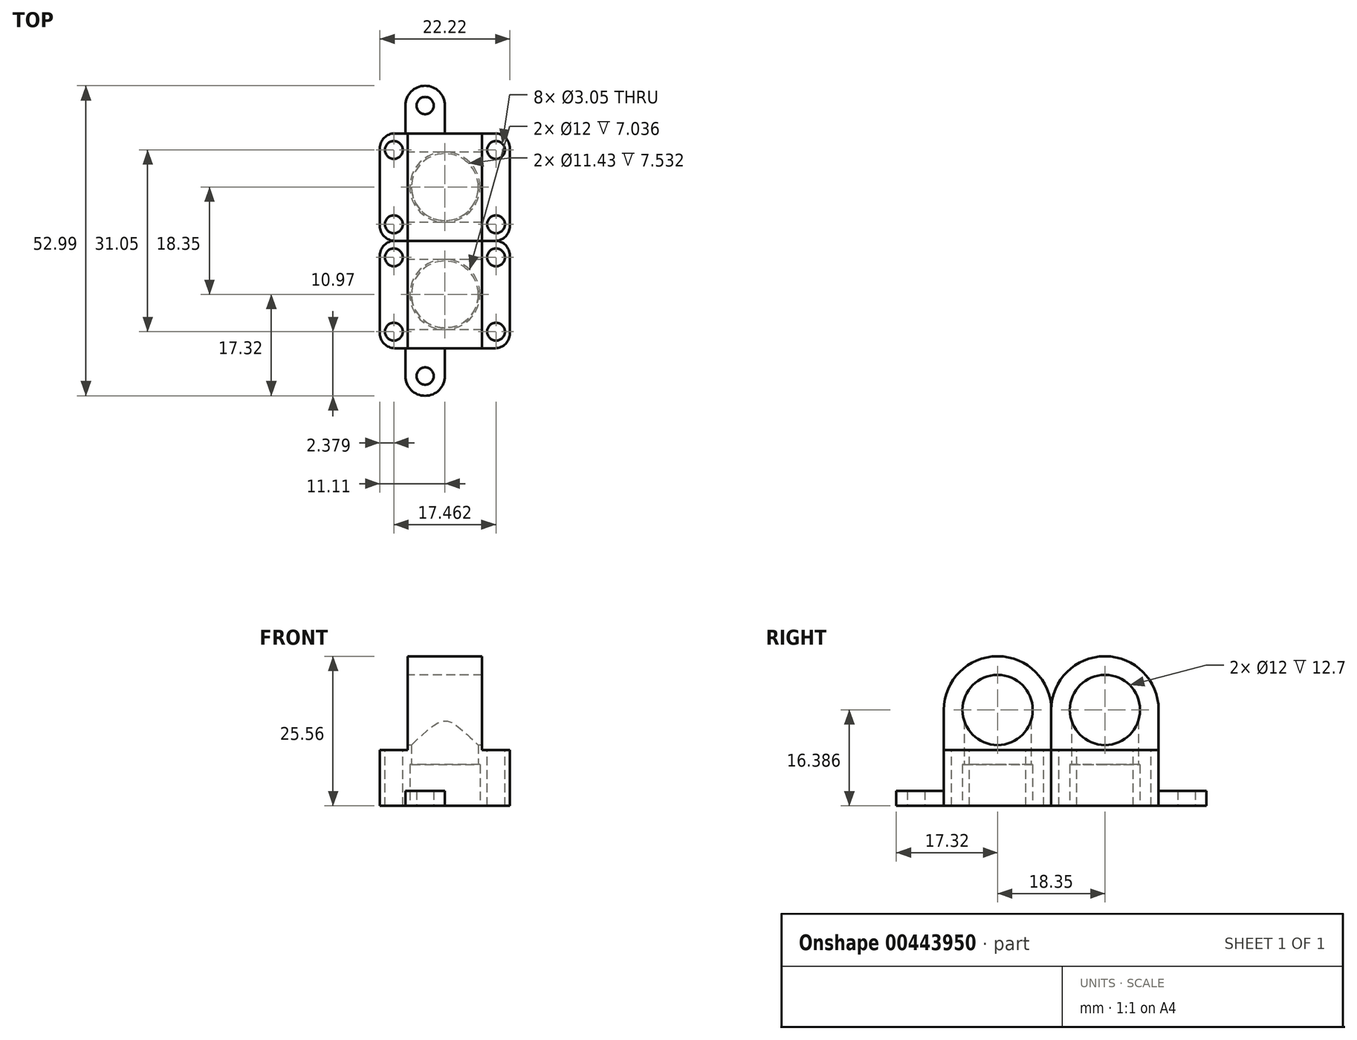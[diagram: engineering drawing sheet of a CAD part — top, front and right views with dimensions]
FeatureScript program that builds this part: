
annotation { "Feature Type Name" : "Feature", "Feature Type Description" : "" }
export const myFeature = defineFeature(function(context is Context, id is Id, definition is map)
    precondition{}
    {
        {
            var Q0;
            Q0=qCreatedBy(makeId("Top.planeOp"),FACE);
            var sketch = newSketch(context, id + "F0", { "sketchPlane" : qUnion([Q0])});
            skCircle(sketch, "E0", {"center": v(0, 0) * mm, "radius": 6 * mm});
            skArc(sketch, "E1", {"start": v(0, 9.18) * mm, "mid": v(9.18, 0) * mm, "end": v(0, -9.18) * mm});
            skLineSegment(sketch, "E2", {"start": v(0, 9.18) * mm, "end": v(-11.11, 9.18) * mm});
            skLineSegment(sketch, "E3", {"start": v(-11.11, 9.18) * mm, "end": v(-11.11, -9.18) * mm});
            skLineSegment(sketch, "E4", {"start": v(-11.11, -9.18) * mm, "end": v(0, -9.18) * mm});
            skSolve(sketch);
        }
        {
            var Q0;
            Q0=qSketchRegion(id+"F0",true);
            extrude(context, id + "F1", {"entities" : qUnion([Q0]), "depth" : 7.04 * mm});
        }
        {
            var Q0;
            Q0=makeQuery(id+"F1.opExtrude","SWEPT_FACE",FACE,{"disambiguationData":[OSD([sQuery(id+"F0.wireOp",EDGE,"E3")])]});
            var sketch = newSketch(context, id + "F2", { "sketchPlane" : qUnion([Q0])});
            skCircle(sketch, "E5", {"center": v(0, 17.8) * mm, "radius": 6 * mm});
            skArc(sketch, "E6", {"start": v(-9.17, 17.8) * mm, "mid": v(0, 26.97) * mm, "end": v(9.17, 17.8) * mm});
            skLineSegment(sketch, "E7", {"start": v(-9.17, 17.8) * mm, "end": v(-9.18, 7.04) * mm});
            skLineSegment(sketch, "E8", {"start": v(-9.18, 7.04) * mm, "end": v(9.17, 7.04) * mm});
            skLineSegment(sketch, "E9", {"start": v(9.17, 7.04) * mm, "end": v(9.17, 17.8) * mm});
            skSolve(sketch);
        }
        {
            var Q0;
            Q0=makeQuery(id+"F1.opExtrude","CAP_FACE",FACE,{"disambiguationData":[OSD([sQuery(id+"F0.wireOp",EDGE,"E0"),sQuery(id+"F0.wireOp",EDGE,"E1"),sQuery(id+"F0.wireOp",EDGE,"E2"),sQuery(id+"F0.wireOp",EDGE,"E3"),sQuery(id+"F0.wireOp",EDGE,"E4")])],"isStart":true});
            var sketch = newSketch(context, id + "F3", { "sketchPlane" : qUnion([Q0])});
            skCircle(sketch, "E10", {"center": v(-3.38, 13.94) * mm, "radius": 1.47 * mm});
            skArc(sketch, "E11", {"start": v(-6.76, 13.94) * mm, "mid": v(-3.38, 17.32) * mm, "end": v(0, 13.94) * mm});
            skLineSegment(sketch, "E12", {"start": v(-6.76, 13.94) * mm, "end": v(-6.76, 9.18) * mm});
            skLineSegment(sketch, "E13", {"start": v(-6.76, 9.18) * mm, "end": v(0, 9.18) * mm});
            skLineSegment(sketch, "E14", {"start": v(0, 9.18) * mm, "end": v(0, 13.94) * mm});
            skSolve(sketch);
        }
        {
            var Q0;
            Q0=qSketchRegion(id+"F3",true);
            extrude(context, id + "F4", {"entities" : qUnion([Q0]), "operationType" : NewBodyOperationType.ADD, "oppositeDirection" : true, "depth" : 2.54 * mm});
        }
        {
            var Q0;
            Q0=makeQuery(id+"F1.opExtrude","CAP_FACE",FACE,{"disambiguationData":[OSD([sQuery(id+"F0.wireOp",EDGE,"E0"),sQuery(id+"F0.wireOp",EDGE,"E1"),sQuery(id+"F0.wireOp",EDGE,"E2"),sQuery(id+"F0.wireOp",EDGE,"E3"),sQuery(id+"F0.wireOp",EDGE,"E4")])],"isStart":false});
            var sketch = newSketch(context, id + "F5", { "sketchPlane" : qUnion([Q0])});
            skLineSegment(sketch, "E15", {"start": v(0, 9.18) * mm, "end": v(11.11, 9.18) * mm});
            skLineSegment(sketch, "E16", {"start": v(11.11, 9.18) * mm, "end": v(11.11, -9.18) * mm});
            skLineSegment(sketch, "E17", {"start": v(11.11, -9.18) * mm, "end": v(0, -9.18) * mm});
            skArc(sketch, "E18", {"start": v(0, -9.18) * mm, "mid": v(9.18, 0) * mm, "end": v(0, 9.18) * mm});
            skSolve(sketch);
        }
        {
            var Q0;
            Q0=qSketchRegion(id+"F5",true);
            var Q1;
            Q1=makeQuery(id+"F4.boolean.opBoolean","MERGE",FACE,{"derivedFrom":[makeQuery(id+"F1.opExtrude","CAP_FACE",FACE,{"disambiguationData":[OSD([sQuery(id+"F0.wireOp",EDGE,"E0"),sQuery(id+"F0.wireOp",EDGE,"E1"),sQuery(id+"F0.wireOp",EDGE,"E2"),sQuery(id+"F0.wireOp",EDGE,"E3"),sQuery(id+"F0.wireOp",EDGE,"E4")])],"isStart":true}),makeQuery(id+"F4.opExtrude","CAP_FACE",FACE,{"disambiguationData":[OSD([sQuery(id+"F3.wireOp",EDGE,"E10"),sQuery(id+"F3.wireOp",EDGE,"E11"),sQuery(id+"F3.wireOp",EDGE,"E12"),sQuery(id+"F3.wireOp",EDGE,"E13"),sQuery(id+"F3.wireOp",EDGE,"E14")])],"isStart":true})]});
            extrude(context, id + "F6", {"entities" : qUnion([Q0]), "operationType" : NewBodyOperationType.ADD, "endBound" : BoundingType.UP_TO_SURFACE, "oppositeDirection" : true, "endBoundEntityFace" : qUnion([Q1]), "depth" : 25.4 * mm});
        }
        {
            var Q0;
            Q0=qCreatedBy(makeId("Right.planeOp"),FACE);
            var sketch = newSketch(context, id + "F7", { "sketchPlane" : qUnion([Q0])});
            skCircle(sketch, "E19", {"center": v(0, 16.39) * mm, "radius": 6 * mm});
            skArc(sketch, "E20", {"start": v(9.18, 16.39) * mm, "mid": v(0, 25.56) * mm, "end": v(-9.18, 16.39) * mm});
            skLineSegment(sketch, "E21", {"start": v(-9.17, 16.39) * mm, "end": v(-9.18, 7.04) * mm});
            skLineSegment(sketch, "E22", {"start": v(-9.18, 7.04) * mm, "end": v(9.18, 7.04) * mm});
            skLineSegment(sketch, "E23", {"start": v(9.18, 7.04) * mm, "end": v(9.18, 16.39) * mm});
            skLineSegment(sketch, "E24.bottom", {"start": v(3, 7.04) * mm, "end": v(-3, 7.04) * mm, "construction": true});
            skLineSegment(sketch, "E24.top", {"start": v(3, 13.39) * mm, "end": v(-3, 13.39) * mm, "construction": true});
            skLineSegment(sketch, "E24.left", {"start": v(3, 7.04) * mm, "end": v(3, 13.39) * mm, "construction": true});
            skLineSegment(sketch, "E24.right", {"start": v(-3, 7.04) * mm, "end": v(-3, 13.39) * mm, "construction": true});
            skPoint(sketch, "E24.middle", {"position": v(0, 10.21) * mm});
            skCircle(sketch, "E25", {"center": v(0, 16.39) * mm, "radius": 3 * mm, "construction": true});
            skSolve(sketch);
        }
        {
            var Q0;
            Q0=qSketchRegion(id+"F7",true);
            extrude(context, id + "F8", {"entities" : qUnion([Q0]), "endBound" : BoundingType.SYMMETRIC, "depth" : 12.7 * mm});
        }
        {
            var Q0;
            Q0=makeQuery(id+"F8.opExtrude","SWEPT_FACE",FACE,{"disambiguationData":[OSD([sQuery(id+"F7.wireOp",EDGE,"E22")])]});
            var sketch = newSketch(context, id + "F9", { "sketchPlane" : qUnion([Q0])});
            skLineSegment(sketch, "E26.bottom", {"start": v(-11.11, 9.17) * mm, "end": v(11.11, 9.17) * mm});
            skLineSegment(sketch, "E26.top", {"start": v(-11.11, -9.17) * mm, "end": v(11.11, -9.17) * mm});
            skLineSegment(sketch, "E26.left", {"start": v(-11.11, 9.17) * mm, "end": v(-11.11, -9.17) * mm});
            skLineSegment(sketch, "E26.right", {"start": v(11.11, 9.17) * mm, "end": v(11.11, -9.17) * mm});
            skPoint(sketch, "E26.middle", {"position": v(0, 0) * mm});
            skSolve(sketch);
        }
        {
            var Q0;
            Q0=qSketchRegion(id+"F9",true);
            extrude(context, id + "F10", {"entities" : qUnion([Q0]), "operationType" : NewBodyOperationType.ADD, "oppositeDirection" : true, "depth" : 2.5 * mm});
        }
        {
            var Q0;
            {var subQ0=sQuery(id+"F9.wireOp",EDGE,"E26.bottom");var subQ3=sQuery(id+"F9.wireOp",EDGE,"E26.top");var subQ4=sQuery(id+"F9.wireOp",EDGE,"E26.left");Q0=makeQuery(id+"F10.boolean.opBoolean","SPLIT",FACE,{"disambiguationData":[TD([makeQuery(id+"F10.opExtrude","SWEPT_FACE",FACE,{"disambiguationData":[OSD([subQ4])]})])],"derivedFrom":makeQuery(id+"F10.opExtrude","CAP_FACE",FACE,{"disambiguationData":[OSD([subQ0,subQ3,subQ4,sQuery(id+"F9.wireOp",EDGE,"E26.right")])],"isStart":false})});}
            var sketch = newSketch(context, id + "F11", { "sketchPlane" : qUnion([Q0])});
            skLineSegment(sketch, "E27", {"start": v(-8.73, 9.17) * mm, "end": v(-8.73, 6.35) * mm, "construction": true});
            skLineSegment(sketch, "E28.bottom", {"start": v(-8.73, 6.35) * mm, "end": v(8.73, 6.35) * mm, "construction": true});
            skLineSegment(sketch, "E28.top", {"start": v(-8.73, -6.35) * mm, "end": v(8.73, -6.35) * mm, "construction": true});
            skLineSegment(sketch, "E28.left", {"start": v(-8.73, 6.35) * mm, "end": v(-8.73, -6.35) * mm, "construction": true});
            skLineSegment(sketch, "E28.right", {"start": v(8.73, 6.35) * mm, "end": v(8.73, -6.35) * mm, "construction": true});
            skPoint(sketch, "E28.middle", {"position": v(0, 0) * mm});
            skCircle(sketch, "E29", {"center": v(-8.73, 6.35) * mm, "radius": 1.52 * mm});
            skCircle(sketch, "E30", {"center": v(-8.73, -6.35) * mm, "radius": 1.52 * mm});
            skCircle(sketch, "E31", {"center": v(8.73, -6.35) * mm, "radius": 1.52 * mm});
            skCircle(sketch, "E32", {"center": v(8.73, 6.35) * mm, "radius": 1.52 * mm});
            skCircle(sketch, "E33", {"center": v(8.73, 6.35) * mm, "radius": 2.29 * mm, "construction": true});
            skSolve(sketch);
        }
        {
            var Q0;
            Q0=qSketchRegion(id+"F11",true);
            extrude(context, id + "F12", {"entities" : qUnion([Q0]), "operationType" : NewBodyOperationType.REMOVE, "endBound" : BoundingType.THROUGH_ALL, "oppositeDirection" : true, "depth" : 25.4 * mm});
        }
        {
            var Q0;
            Q0=makeQuery(id+"F10.opExtrude","SWEPT_EDGE",EDGE,{"disambiguationData":[OSD([sQuery(id+"F9.wireOp",EDGE,"E26.bottom"),sQuery(id+"F9.wireOp",EDGE,"E26.right")])]});
            var Q1;
            Q1=makeQuery(id+"F10.opExtrude","SWEPT_EDGE",EDGE,{"disambiguationData":[OSD([sQuery(id+"F9.wireOp",EDGE,"E26.bottom"),sQuery(id+"F9.wireOp",EDGE,"E26.left")])]});
            var Q2;
            Q2=makeQuery(id+"F10.opExtrude","SWEPT_EDGE",EDGE,{"disambiguationData":[OSD([sQuery(id+"F9.wireOp",EDGE,"E26.top"),sQuery(id+"F9.wireOp",EDGE,"E26.right")])]});
            var Q3;
            Q3=makeQuery(id+"F10.opExtrude","SWEPT_EDGE",EDGE,{"disambiguationData":[OSD([sQuery(id+"F9.wireOp",EDGE,"E26.top"),sQuery(id+"F9.wireOp",EDGE,"E26.left")])]});
            var Q4;
            Q4=makeQuery(id+"F1.opExtrude","SWEPT_EDGE",EDGE,{"disambiguationData":[OSD([sQuery(id+"F0.wireOp",EDGE,"E2"),sQuery(id+"F0.wireOp",EDGE,"E3")])]});
            var Q5;
            Q5=makeQuery(id+"F6.opExtrude","SWEPT_EDGE",EDGE,{"disambiguationData":[OSD([sQuery(id+"F5.wireOp",EDGE,"E15"),sQuery(id+"F5.wireOp",EDGE,"E16")])]});
            var Q6;
            Q6=makeQuery(id+"F6.opExtrude","SWEPT_EDGE",EDGE,{"disambiguationData":[OSD([sQuery(id+"F5.wireOp",EDGE,"E16"),sQuery(id+"F5.wireOp",EDGE,"E17")])]});
            var Q7;
            Q7=makeQuery(id+"F1.opExtrude","SWEPT_EDGE",EDGE,{"disambiguationData":[OSD([sQuery(id+"F0.wireOp",EDGE,"E3"),sQuery(id+"F0.wireOp",EDGE,"E4")])]});
            fillet(context, id + "F13", {"entities" : qUnion([Q0, Q1, Q2, Q3, Q4, Q5, Q6, Q7]), "radius" : 2.54 * mm, "tangentPropagation" : true, "allowEdgeOverflow" : false});
        }
        {
            var Q0;
            Q0=makeQuery(id+"F10.boolean.opBoolean","MERGE",FACE,{"derivedFrom":[makeQuery(id+"F8.opExtrude","SWEPT_FACE",FACE,{"disambiguationData":[OSD([sQuery(id+"F7.wireOp",EDGE,"E22")])]}),makeQuery(id+"F10.opExtrude","CAP_FACE",FACE,{"disambiguationData":[OSD([sQuery(id+"F9.wireOp",EDGE,"E26.bottom"),sQuery(id+"F9.wireOp",EDGE,"E26.top"),sQuery(id+"F9.wireOp",EDGE,"E26.left"),sQuery(id+"F9.wireOp",EDGE,"E26.right")])],"isStart":true})]});
            var sketch = newSketch(context, id + "F14", { "sketchPlane" : qUnion([Q0])});
            skCircle(sketch, "E34", {"center": v(0, 0) * mm, "radius": 5.72 * mm});
            skSolve(sketch);
        }
        {
            var Q0;
            Q0=qSketchRegion(id+"F14",true);
            extrude(context, id + "F15", {"entities" : qUnion([Q0]), "operationType" : NewBodyOperationType.REMOVE, "endBound" : BoundingType.UP_TO_NEXT, "oppositeDirection" : true, "depth" : 25.4 * mm});
        }
        {
            var Q0;
            Q0=makeQuery(id+"F1.opExtrude","SWEPT_BODY",BODY,{"disambiguationData":[OSD([sQuery(id+"F0.wireOp",EDGE,"E0"),sQuery(id+"F0.wireOp",EDGE,"E1"),sQuery(id+"F0.wireOp",EDGE,"E2"),sQuery(id+"F0.wireOp",EDGE,"E3"),sQuery(id+"F0.wireOp",EDGE,"E4")])]});
            var Q1;
            Q1=makeQuery(id+"F8.opExtrude","SWEPT_BODY",BODY,{"disambiguationData":[OSD([sQuery(id+"F7.wireOp",EDGE,"E19"),sQuery(id+"F7.wireOp",EDGE,"E20"),sQuery(id+"F7.wireOp",EDGE,"E21"),sQuery(id+"F7.wireOp",EDGE,"E22"),sQuery(id+"F7.wireOp",EDGE,"E23")])]});
            var Q2;
            Q2=makeQuery(id+"FeltiWKGKCvlbtT_1.boolean.opBoolean","MERGE",FACE,{"derivedFrom":[makeQuery(id+"FC8TW2MyN47ePtH_1.boolean.opBoolean","MERGE",FACE,{"derivedFrom":[makeQuery(id+"F1.opExtrude","SWEPT_FACE",FACE,{"disambiguationData":[OSD([sQuery(id+"F0.wireOp",EDGE,"E2")])]}),makeQuery(id+"FC8TW2MyN47ePtH_1.opExtrude","SWEPT_FACE",FACE,{"disambiguationData":[OSD([sQuery(id+"F2.wireOp",EDGE,"E7")])]})]}),makeQuery(id+"FeltiWKGKCvlbtT_1.opExtrude","CAP_FACE",FACE,{"disambiguationData":[OSD([sQuery(id+"FoJXFF1IQi9VodQ_1.wireOp",EDGE,"BADv9P94-FekH-q6qW-Nt0h-muAZdhJqY5QK"),sQuery(id+"FoJXFF1IQi9VodQ_1.wireOp",EDGE,"YD8KbyGX-3SDk-gQUb-EbM9-0zymLiGli5nf"),sQuery(id+"FoJXFF1IQi9VodQ_1.wireOp",EDGE,"xjQTqq31-lGEv-446r-anc1-TYDgfewutVNj")])],"isStart":true})]});
            mirror(context, id + "F16", {"entities" : qUnion([Q0, Q1]), "mirrorPlane" : qUnion([Q2])});
        }
    });
